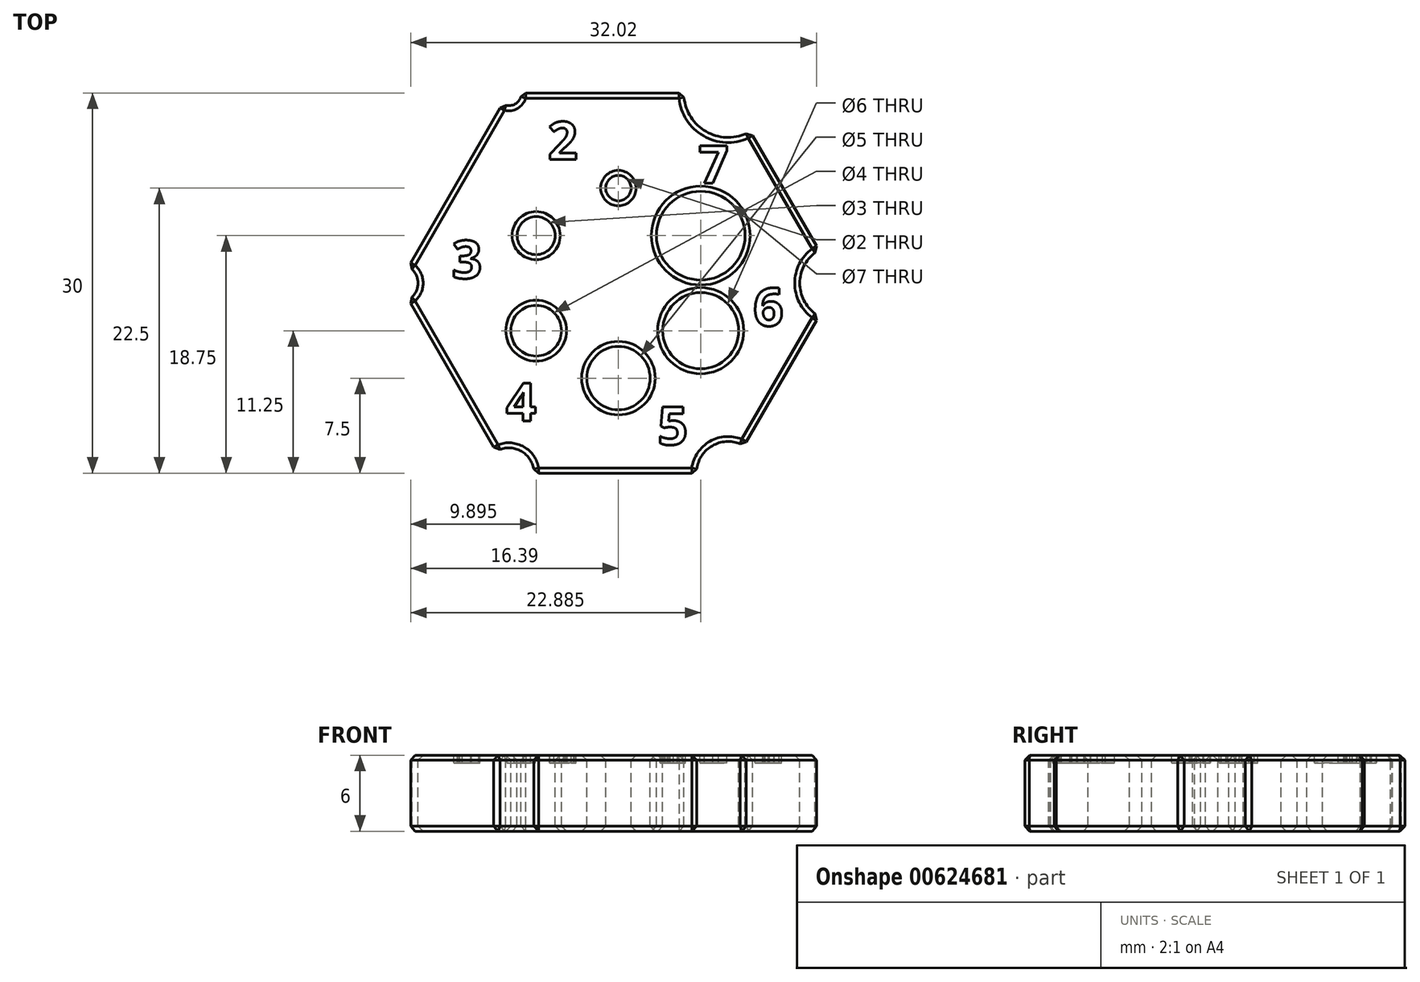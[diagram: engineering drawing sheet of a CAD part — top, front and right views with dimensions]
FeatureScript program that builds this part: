
annotation { "Feature Type Name" : "Feature", "Feature Type Description" : "" }
export const myFeature = defineFeature(function(context is Context, id is Id, definition is map)
    precondition{}
    {
        {
            var Q0;
            Q0=qCreatedBy(makeId("Top.planeOp"),FACE);
            var sketch = newSketch(context, id + "F0", { "sketchPlane" : qUnion([Q0])});
            skCircle(sketch, "E0.cCircle", {"center": v(0, 0) * mm, "radius": 15 * mm, "construction": true});
            skLineSegment(sketch, "E0.0", {"start": v(-8.66, 15) * mm, "end": v(8.66, 15) * mm});
            skLineSegment(sketch, "E0.1", {"start": v(8.66, 15) * mm, "end": v(17.32, 0) * mm});
            skLineSegment(sketch, "E0.2", {"start": v(17.32, 0) * mm, "end": v(8.66, -15) * mm});
            skLineSegment(sketch, "E0.3", {"start": v(8.66, -15) * mm, "end": v(-8.66, -15) * mm});
            skLineSegment(sketch, "E0.4", {"start": v(-8.66, -15) * mm, "end": v(-17.32, 0) * mm});
            skLineSegment(sketch, "E0.5", {"start": v(-17.32, 0) * mm, "end": v(-8.66, 15) * mm});
            skPoint(sketch, "E0.0.midPoint", {"position": v(0, 15) * mm});
            skCircle(sketch, "E1", {"center": v(-8.66, 15) * mm, "radius": 1 * mm});
            skCircle(sketch, "E2", {"center": v(-17.32, 0) * mm, "radius": 1.5 * mm});
            skCircle(sketch, "E3", {"center": v(-8.66, -15) * mm, "radius": 2 * mm});
            skCircle(sketch, "E4", {"center": v(8.66, -15) * mm, "radius": 2.5 * mm});
            skCircle(sketch, "E5", {"center": v(17.32, 0) * mm, "radius": 3 * mm});
            skCircle(sketch, "E6", {"center": v(8.66, 15) * mm, "radius": 3.5 * mm});
            skCircle(sketch, "E7.cCircle", {"center": v(0, 0) * mm, "radius": 6.5 * mm, "construction": true});
            skLineSegment(sketch, "E7.0", {"start": v(0, 7.5) * mm, "end": v(6.5, 3.75) * mm, "construction": true});
            skLineSegment(sketch, "E7.1", {"start": v(6.5, 3.75) * mm, "end": v(6.5, -3.75) * mm, "construction": true});
            skLineSegment(sketch, "E7.2", {"start": v(6.5, -3.75) * mm, "end": v(0, -7.5) * mm, "construction": true});
            skLineSegment(sketch, "E7.3", {"start": v(0, -7.5) * mm, "end": v(-6.5, -3.75) * mm, "construction": true});
            skLineSegment(sketch, "E7.4", {"start": v(-6.5, -3.75) * mm, "end": v(-6.5, 3.75) * mm, "construction": true});
            skLineSegment(sketch, "E7.5", {"start": v(-6.5, 3.75) * mm, "end": v(0, 7.5) * mm, "construction": true});
            skPoint(sketch, "E7.0.midPoint", {"position": v(3.25, 5.63) * mm});
            skCircle(sketch, "E8", {"center": v(0, 7.5) * mm, "radius": 1 * mm});
            skCircle(sketch, "E9", {"center": v(-6.5, 3.75) * mm, "radius": 1.5 * mm});
            skCircle(sketch, "E10", {"center": v(-6.5, -3.75) * mm, "radius": 2 * mm});
            skCircle(sketch, "E11", {"center": v(0, -7.5) * mm, "radius": 2.5 * mm});
            skCircle(sketch, "E12", {"center": v(6.5, -3.75) * mm, "radius": 3 * mm});
            skCircle(sketch, "E13", {"center": v(6.5, 3.75) * mm, "radius": 3.5 * mm});
            skText(sketch, "E14", { "text": "2", "fontName": "OpenSans-Bold.ttf"});
            skText(sketch, "E15", { "text": "3", "fontName": "OpenSans-Bold.ttf"});
            skText(sketch, "E16", { "text": "4\n", "fontName": "OpenSans-Bold.ttf"});
            skText(sketch, "E17", { "text": "5", "fontName": "OpenSans-Bold.ttf"});
            skText(sketch, "E18", { "text": "6", "fontName": "OpenSans-Bold.ttf"});
            skText(sketch, "E19", { "text": "7", "fontName": "OpenSans-Bold.ttf"});
            skLineSegment(sketch, "E20", {"start": v(0, -7.5) * mm, "end": v(8.66, -15) * mm, "construction": true});
            skLineSegment(sketch, "E21", {"start": v(6.5, -3.75) * mm, "end": v(17.32, 0) * mm, "construction": true});
            skLineSegment(sketch, "E22", {"start": v(6.5, 3.75) * mm, "end": v(8.66, 15) * mm, "construction": true});
            skLineSegment(sketch, "E23", {"start": v(-8.66, -15) * mm, "end": v(-6.5, -3.75) * mm, "construction": true});
            skLineSegment(sketch, "E24", {"start": v(-6.5, 3.75) * mm, "end": v(-17.32, 0) * mm, "construction": true});
            skLineSegment(sketch, "E25", {"start": v(0, 7.5) * mm, "end": v(-8.66, 15) * mm, "construction": true});
            skPoint(sketch, "E26", {"position": v(-4.33, 11.25) * mm});
            skPoint(sketch, "E27", {"position": v(7.58, 9.38) * mm});
            skPoint(sketch, "E28", {"position": v(11.9, -1.87) * mm});
            skPoint(sketch, "E29", {"position": v(4.33, -11.25) * mm});
            skPoint(sketch, "E30", {"position": v(-7.58, -9.38) * mm});
            skPoint(sketch, "E31", {"position": v(-11.9, 1.87) * mm});
            skPoint(sketch, "E32", {"position": v(-11.9, 1.88) * mm});
            const initialGuessF0  = {"E14": [-0.00559, 0.00975, 1, 0, 0.003], "E15": [-0.01315, 0.00038, 1, 0, 0.003], "E16": [-0.00887, -0.01088, 1, 0, 0.003], "E17": [0.0031, -0.01275, 1, 0, 0.003], "E18": [0.01065, -0.00337, 1, 0, 0.003], "E19": [0.00632, 0.00788, 1, 0, 0.003]};
            skSetInitialGuess(sketch, initialGuessF0);
            skSolve(sketch);
        }
        {
            var Q0;
            Q0=makeQuery(id+"F0.imprint","IMPRINT",FACE,{"disambiguationData":[TD([[makeQuery(id+"F0.imprint","IMPRINT",EDGE,{"derivedFrom":sQuery(id+"F0.wireOp",EDGE,"E8")}),-1.0]])]});
            var Q1;
            Q1=makeQuery(id+"F0.imprint","IMPRINT",FACE,{"disambiguationData":[TD([[makeQuery(id+"F0.imprint","IMPRINT",EDGE,{"derivedFrom":sQuery(id+"F0.wireOp",EDGE,"E14.sketch_text.stroke-0")}),-1.0]])]});
            var Q2;
            Q2=makeQuery(id+"F0.imprint","IMPRINT",FACE,{"disambiguationData":[TD([[makeQuery(id+"F0.imprint","IMPRINT",EDGE,{"derivedFrom":sQuery(id+"F0.wireOp",EDGE,"E19.sketch_text.stroke-0")}),-1.0]])]});
            var Q3;
            Q3=makeQuery(id+"F0.imprint","IMPRINT",FACE,{"disambiguationData":[TD([[makeQuery(id+"F0.imprint","IMPRINT",EDGE,{"derivedFrom":sQuery(id+"F0.wireOp",EDGE,"E18.sketch_text.stroke-0")}),-1.0]])]});
            var Q4;
            Q4=makeQuery(id+"F0.imprint","IMPRINT",FACE,{"disambiguationData":[TD([[makeQuery(id+"F0.imprint","IMPRINT",EDGE,{"derivedFrom":sQuery(id+"F0.wireOp",EDGE,"E18.sketch_text.stroke-17")}),1.0]])]});
            var Q5;
            Q5=makeQuery(id+"F0.imprint","IMPRINT",FACE,{"disambiguationData":[TD([[makeQuery(id+"F0.imprint","IMPRINT",EDGE,{"derivedFrom":sQuery(id+"F0.wireOp",EDGE,"E15.sketch_text.stroke-0")}),-1.0]])]});
            var Q6;
            Q6=makeQuery(id+"F0.imprint","IMPRINT",FACE,{"disambiguationData":[TD([[makeQuery(id+"F0.imprint","IMPRINT",EDGE,{"derivedFrom":sQuery(id+"F0.wireOp",EDGE,"E16.sketch_text.stroke-0")}),-1.0]])]});
            var Q7;
            Q7=makeQuery(id+"F0.imprint","IMPRINT",FACE,{"disambiguationData":[TD([[makeQuery(id+"F0.imprint","IMPRINT",EDGE,{"derivedFrom":sQuery(id+"F0.wireOp",EDGE,"E17.sketch_text.stroke-0")}),-1.0]])]});
            var Q8;
            Q8=makeQuery(id+"F0.imprint","IMPRINT",FACE,{"disambiguationData":[TD([[makeQuery(id+"F0.imprint","IMPRINT",EDGE,{"derivedFrom":sQuery(id+"F0.wireOp",EDGE,"E16.sketch_text.stroke-11")}),1.0]])]});
            extrude(context, id + "F1", {"entities" : qUnion([Q0, Q1, Q2, Q3, Q4, Q5, Q6, Q7, Q8]), "oppositeDirection" : true, "depth" : 6 * mm, "offsetDistance" : 25 * mm});
        }
        {
            var Q0;
            Q0=makeQuery(id+"F0.imprint","IMPRINT",FACE,{"disambiguationData":[TD([[makeQuery(id+"F0.imprint","IMPRINT",EDGE,{"derivedFrom":sQuery(id+"F0.wireOp",EDGE,"E14.sketch_text.stroke-0")}),-1.0]])]});
            var Q1;
            Q1=makeQuery(id+"F0.imprint","IMPRINT",FACE,{"disambiguationData":[TD([[makeQuery(id+"F0.imprint","IMPRINT",EDGE,{"derivedFrom":sQuery(id+"F0.wireOp",EDGE,"E19.sketch_text.stroke-0")}),-1.0]])]});
            var Q2;
            Q2=makeQuery(id+"F0.imprint","IMPRINT",FACE,{"disambiguationData":[TD([[makeQuery(id+"F0.imprint","IMPRINT",EDGE,{"derivedFrom":sQuery(id+"F0.wireOp",EDGE,"E15.sketch_text.stroke-0")}),-1.0]])]});
            var Q3;
            Q3=makeQuery(id+"F0.imprint","IMPRINT",FACE,{"disambiguationData":[TD([[makeQuery(id+"F0.imprint","IMPRINT",EDGE,{"derivedFrom":sQuery(id+"F0.wireOp",EDGE,"E16.sketch_text.stroke-0")}),-1.0]])]});
            var Q4;
            Q4=makeQuery(id+"F0.imprint","IMPRINT",FACE,{"disambiguationData":[TD([[makeQuery(id+"F0.imprint","IMPRINT",EDGE,{"derivedFrom":sQuery(id+"F0.wireOp",EDGE,"E17.sketch_text.stroke-0")}),-1.0]])]});
            var Q5;
            Q5=makeQuery(id+"F0.imprint","IMPRINT",FACE,{"disambiguationData":[TD([[makeQuery(id+"F0.imprint","IMPRINT",EDGE,{"derivedFrom":sQuery(id+"F0.wireOp",EDGE,"E18.sketch_text.stroke-0")}),-1.0]])]});
            extrude(context, id + "F2", {"entities" : qUnion([Q0, Q1, Q2, Q3, Q4, Q5]), "operationType" : NewBodyOperationType.REMOVE, "oppositeDirection" : true, "depth" : 0.6 * mm, "offsetDistance" : 25 * mm});
        }
        {
            var Q0;
            Q0=makeQuery(id+"F1.opExtrude","SWEPT_FACE",FACE,{"disambiguationData":[OSD([sQuery(id+"F0.wireOp",EDGE,"E0.4")])]});
            var Q1;
            Q1=makeQuery(id+"F1.opExtrude","SWEPT_FACE",FACE,{"disambiguationData":[OSD([sQuery(id+"F0.wireOp",EDGE,"E0.3")])]});
            var Q2;
            Q2=makeQuery(id+"F1.opExtrude","SWEPT_FACE",FACE,{"disambiguationData":[OSD([sQuery(id+"F0.wireOp",EDGE,"E3")])]});
            var Q3;
            Q3=makeQuery(id+"F1.opExtrude","SWEPT_FACE",FACE,{"disambiguationData":[OSD([sQuery(id+"F0.wireOp",EDGE,"E4")])]});
            var Q4;
            Q4=makeQuery(id+"F1.opExtrude","SWEPT_FACE",FACE,{"disambiguationData":[OSD([sQuery(id+"F0.wireOp",EDGE,"E0.2")])]});
            var Q5;
            Q5=makeQuery(id+"F1.opExtrude","SWEPT_FACE",FACE,{"disambiguationData":[OSD([sQuery(id+"F0.wireOp",EDGE,"E5")])]});
            var Q6;
            Q6=makeQuery(id+"F1.opExtrude","SWEPT_FACE",FACE,{"disambiguationData":[OSD([sQuery(id+"F0.wireOp",EDGE,"E0.1")])]});
            var Q7;
            Q7=makeQuery(id+"F1.opExtrude","SWEPT_FACE",FACE,{"disambiguationData":[OSD([sQuery(id+"F0.wireOp",EDGE,"E6")])]});
            var Q8;
            Q8=makeQuery(id+"F1.opExtrude","SWEPT_FACE",FACE,{"disambiguationData":[OSD([sQuery(id+"F0.wireOp",EDGE,"E0.0")])]});
            var Q9;
            Q9=makeQuery(id+"F1.opExtrude","SWEPT_FACE",FACE,{"disambiguationData":[OSD([sQuery(id+"F0.wireOp",EDGE,"E1")])]});
            var Q10;
            Q10=makeQuery(id+"F1.opExtrude","SWEPT_FACE",FACE,{"disambiguationData":[OSD([sQuery(id+"F0.wireOp",EDGE,"E0.5")])]});
            var Q11;
            Q11=makeQuery(id+"F1.opExtrude","SWEPT_FACE",FACE,{"disambiguationData":[OSD([sQuery(id+"F0.wireOp",EDGE,"E2")])]});
            var Q12;
            Q12=makeQuery(id+"F1.opExtrude","SWEPT_FACE",FACE,{"disambiguationData":[OSD([sQuery(id+"F0.wireOp",EDGE,"E12")])]});
            var Q13;
            Q13=makeQuery(id+"F1.opExtrude","SWEPT_FACE",FACE,{"disambiguationData":[OSD([sQuery(id+"F0.wireOp",EDGE,"E11")])]});
            var Q14;
            Q14=makeQuery(id+"F1.opExtrude","SWEPT_FACE",FACE,{"disambiguationData":[OSD([sQuery(id+"F0.wireOp",EDGE,"E10")])]});
            var Q15;
            Q15=makeQuery(id+"F1.opExtrude","SWEPT_FACE",FACE,{"disambiguationData":[OSD([sQuery(id+"F0.wireOp",EDGE,"E9")])]});
            var Q16;
            Q16=makeQuery(id+"F1.opExtrude","SWEPT_FACE",FACE,{"disambiguationData":[OSD([sQuery(id+"F0.wireOp",EDGE,"E8")])]});
            var Q17;
            Q17=makeQuery(id+"F1.opExtrude","SWEPT_FACE",FACE,{"disambiguationData":[OSD([sQuery(id+"F0.wireOp",EDGE,"E13")])]});
            chamfer(context, id + "F3", {"entities" : qUnion([Q0, Q1, Q2, Q3, Q4, Q5, Q6, Q7, Q8, Q9, Q10, Q11, Q12, Q13, Q14, Q15, Q16, Q17]), "width" : 0.4 * mm, "tangentPropagation" : true});
        }
    });
